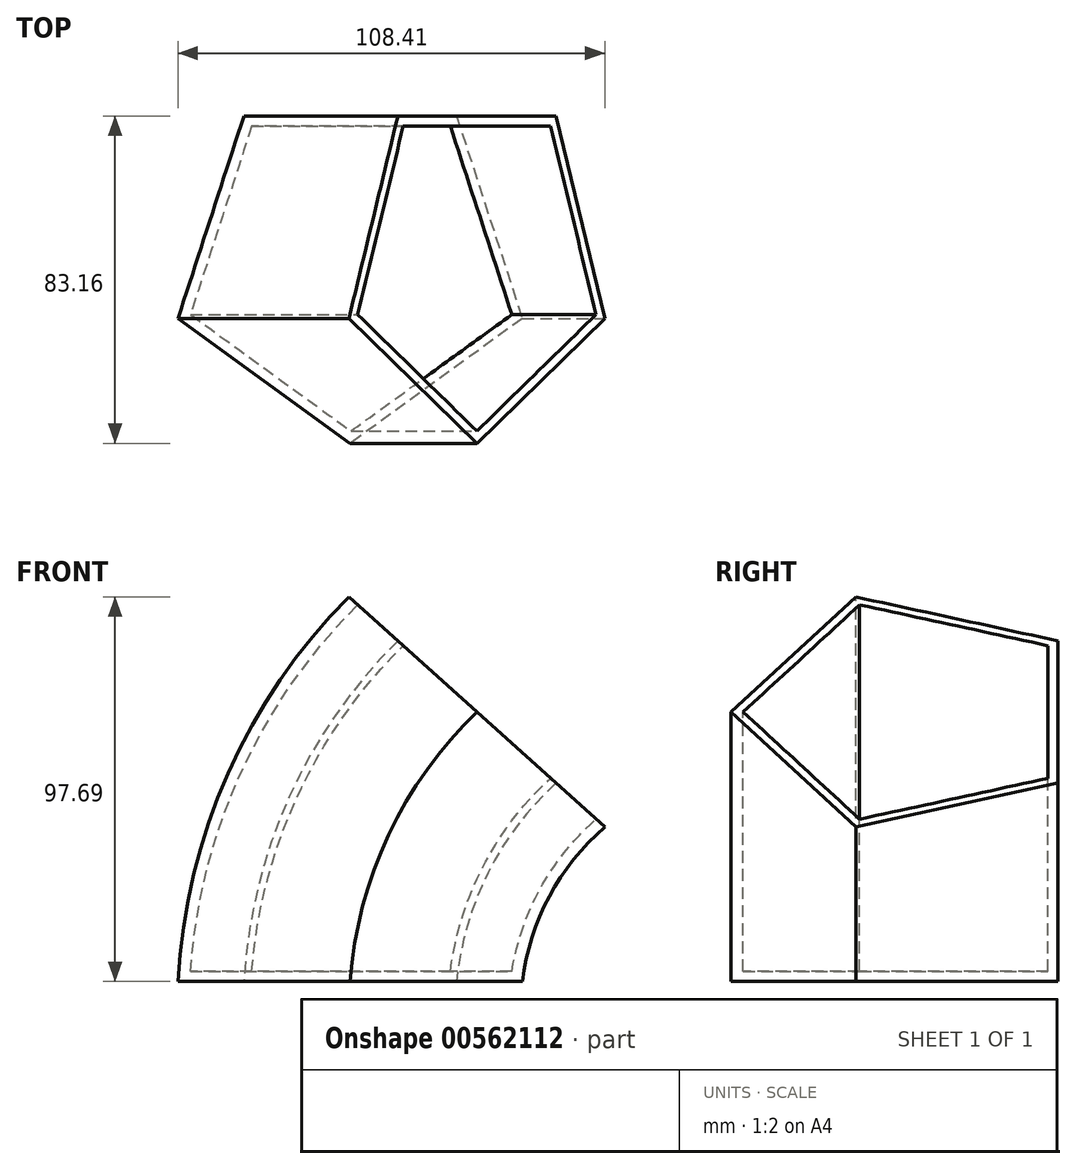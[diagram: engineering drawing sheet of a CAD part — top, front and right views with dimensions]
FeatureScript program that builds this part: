
annotation { "Feature Type Name" : "Feature", "Feature Type Description" : "" }
export const myFeature = defineFeature(function(context is Context, id is Id, definition is map)
    precondition{}
    {
        {
            var Q0;
            Q0=qCreatedBy(makeId("Top.planeOp"),FACE);
            var sketch = newSketch(context, id + "F0", { "sketchPlane" : qUnion([Q0])});
            skCircle(sketch, "E0.cCircle", {"center": v(0, 0) * mm, "radius": 37.2 * mm, "construction": true});
            skLineSegment(sketch, "E0.0", {"start": v(-27.02, 37.2) * mm, "end": v(27.02, 37.2) * mm});
            skLineSegment(sketch, "E0.1", {"start": v(27.02, 37.2) * mm, "end": v(43.72, -14.2) * mm});
            skLineSegment(sketch, "E0.2", {"start": v(43.72, -14.2) * mm, "end": v(0, -45.97) * mm});
            skLineSegment(sketch, "E0.3", {"start": v(0, -45.97) * mm, "end": v(-43.72, -14.2) * mm});
            skLineSegment(sketch, "E0.4", {"start": v(-43.72, -14.2) * mm, "end": v(-27.02, 37.2) * mm});
            skPoint(sketch, "E0.0.midPoint", {"position": v(0, 37.2) * mm});
            skSolve(sketch);
        }
        {
            var Q0;
            Q0=qCreatedBy(makeId("Front.planeOp"),FACE);
            var sketch = newSketch(context, id + "F1", { "sketchPlane" : qUnion([Q0])});
            skArc(sketch, "E1", {"start": v(32.2, 68.45) * mm, "mid": v(9.76, 37.2) * mm, "end": v(0, 0) * mm});
            skSolve(sketch);
        }
        {
            var Q0;
            Q0=makeQuery(id+"F0.imprint","IMPRINT",FACE,{"disambiguationData":[TD([[makeQuery(id+"F0.imprint","IMPRINT",EDGE,{"derivedFrom":sQuery(id+"F0.wireOp",EDGE,"E0.0")}),-1.0]])]});
            var Q1;
            Q1=sQuery(id+"F1.wireOp",EDGE,"E1");
            sweep(context, id + "F2", {"profiles" : qUnion([Q0]), "path" : qUnion([Q1])});
        }
        {
            var Q0;
            Q0=makeQuery(id+"F2.opSweep","CAP_FACE",FACE,{"disambiguationData":[OSD([sQuery(id+"F0.wireOp",EDGE,"E0.0"),sQuery(id+"F0.wireOp",EDGE,"E0.1"),sQuery(id+"F0.wireOp",EDGE,"E0.2"),sQuery(id+"F0.wireOp",EDGE,"E0.3"),sQuery(id+"F0.wireOp",EDGE,"E0.4"),sQuery(id+"F1.wireOp",VERTEX,"E1.start")])],"isStart":false});
            shell(context, id + "F3", {"entities" : qUnion([Q0]), "thickness" : 2.54 * mm});
        }
    });
